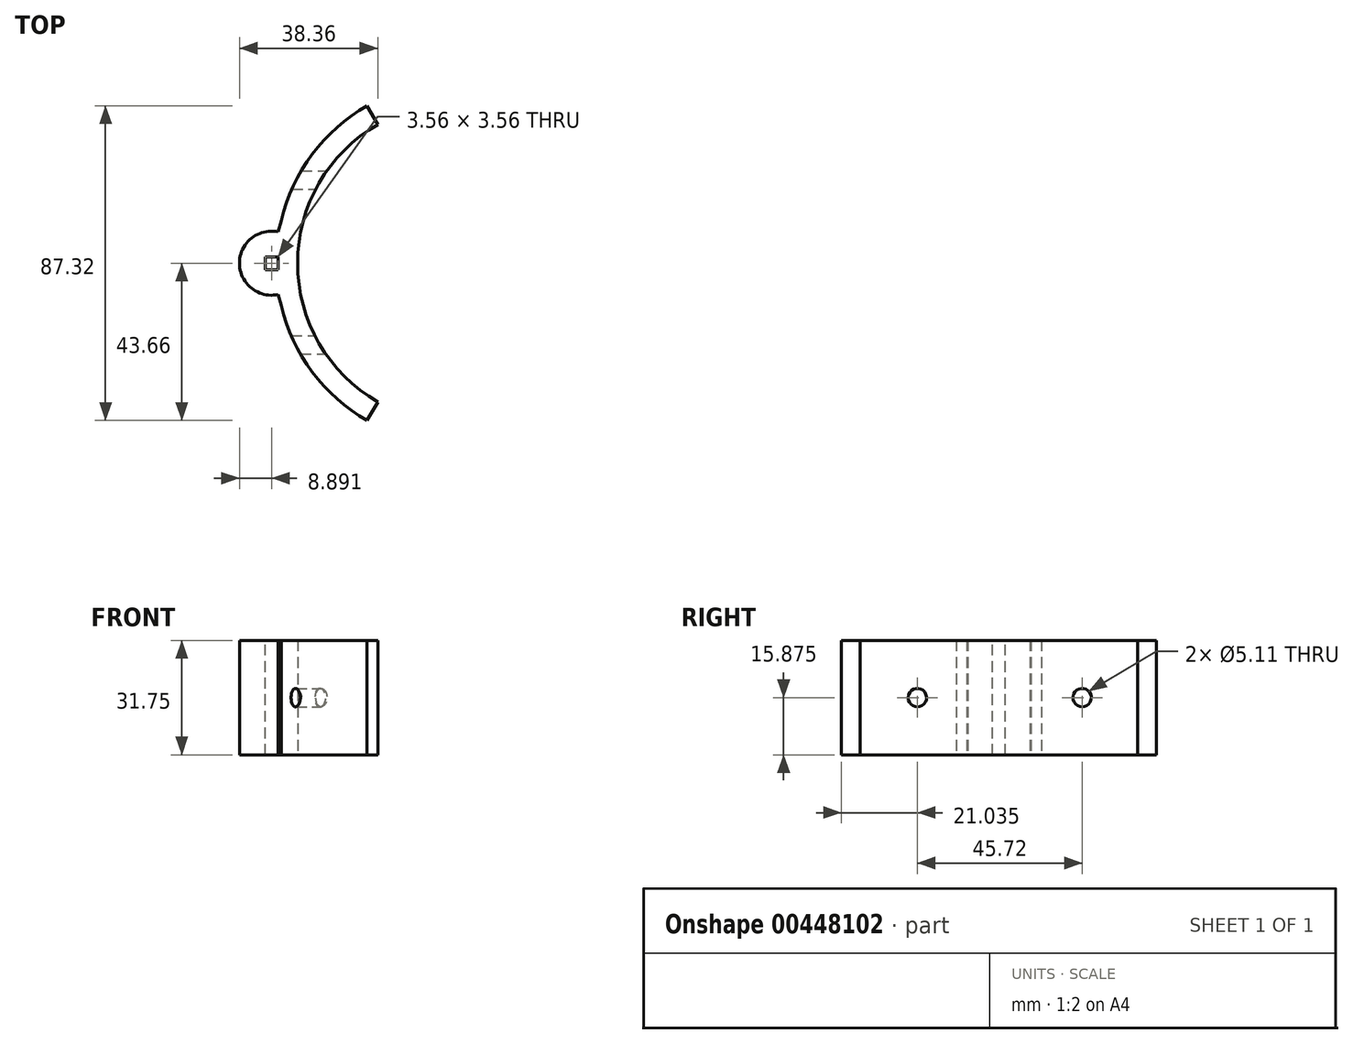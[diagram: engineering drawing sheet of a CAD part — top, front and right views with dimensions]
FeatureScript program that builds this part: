
annotation { "Feature Type Name" : "Feature", "Feature Type Description" : "" }
export const myFeature = defineFeature(function(context is Context, id is Id, definition is map)
    precondition{}
    {
        {
            var Q0;
            Q0=qCreatedBy(makeId("Top.planeOp"),FACE);
            var sketch = newSketch(context, id + "F0", { "sketchPlane" : qUnion([Q0])});
            skArc(sketch, "E0", {"start": v(-22.22, 38.5) * mm, "mid": v(-44.45, 0) * mm, "end": v(-22.22, -38.5) * mm});
            skLineSegment(sketch, "E1", {"start": v(-44.45, 0) * mm, "end": v(-22.23, 0) * mm, "construction": true});
            skPoint(sketch, "E2.start.orphan", {"position": v(-22.23, 0) * mm});
            skArc(sketch, "E3.0", {"start": v(-25.2, 43.66) * mm, "mid": v(-40.4, 30.16) * mm, "end": v(-49.03, 11.75) * mm});
            skLineSegment(sketch, "E4", {"start": v(-25.2, 43.66) * mm, "end": v(-22.22, 38.5) * mm});
            skLineSegment(sketch, "E5", {"start": v(-22.22, -38.5) * mm, "end": v(-25.2, -43.66) * mm});
            skCircle(sketch, "E6", {"center": v(-51.69, 0) * mm, "radius": 1.27 * mm});
            skPoint(sketch, "E6.centerSnap0", {"position": v(-50.42, 0) * mm});
            skLineSegment(sketch, "E7", {"start": v(-49.8, 8.69) * mm, "end": v(-49.03, 11.75) * mm});
            skLineSegment(sketch, "E8", {"start": v(-49.8, -8.69) * mm, "end": v(-49.03, -11.75) * mm});
            skArc(sketch, "E9.trimOffspring", {"start": v(-49.03, -11.75) * mm, "mid": v(-40.4, -30.16) * mm, "end": v(-25.2, -43.66) * mm});
            skArc(sketch, "E10.0", {"start": v(-49.8, 8.69) * mm, "mid": v(-60.58, 0) * mm, "end": v(-49.8, -8.69) * mm});
            skPoint(sketch, "E11.orphan", {"position": v(-51.69, 1.27) * mm});
            skPoint(sketch, "E12.orphan", {"position": v(-51.69, -1.27) * mm});
            skSolve(sketch);
        }
        {
            var Q0;
            Q0 = qSketchRegion(id + "F0", true);
            extrude(context, id + "F1", {"entities" : qUnion([Q0]), "depth" : 31.75 * mm});
        }
        {
            var Q0;
            Q0=makeQuery(id+"F1.opExtrude","CAP_FACE",FACE,{"disambiguationData":[OSD([sQuery(id+"F0.wireOp",EDGE,"E0"),sQuery(id+"F0.wireOp",EDGE,"E3.0"),sQuery(id+"F0.wireOp",EDGE,"E4"),sQuery(id+"F0.wireOp",EDGE,"E5"),sQuery(id+"F0.wireOp",EDGE,"E6"),sQuery(id+"F0.wireOp",EDGE,"E7"),sQuery(id+"F0.wireOp",EDGE,"E8"),sQuery(id+"F0.wireOp",EDGE,"E9.trimOffspring"),sQuery(id+"F0.wireOp",EDGE,"E10.0")])],"isStart":false});
            var sketch = newSketch(context, id + "F2", { "sketchPlane" : qUnion([Q0])});
            skLineSegment(sketch, "E13.bottom", {"start": v(-49.91, -1.78) * mm, "end": v(-53.47, -1.78) * mm});
            skLineSegment(sketch, "E13.top", {"start": v(-49.91, 1.78) * mm, "end": v(-53.47, 1.78) * mm});
            skLineSegment(sketch, "E13.left", {"start": v(-49.91, -1.78) * mm, "end": v(-49.91, 1.78) * mm});
            skLineSegment(sketch, "E13.right", {"start": v(-53.47, -1.78) * mm, "end": v(-53.47, 1.78) * mm});
            skPoint(sketch, "E13.middle", {"position": v(-51.69, 0) * mm});
            skSolve(sketch);
        }
        {
            var Q0;
            Q0=makeQuery(id+"F2.imprint","IMPRINT",FACE,{"disambiguationData":[TD([[makeQuery(id+"F2.imprint","IMPRINT",EDGE,{"derivedFrom":sQuery(id+"F2.wireOp",EDGE,"E13.bottom")}),-1.0]])]});
            extrude(context, id + "F3", {"entities" : qUnion([Q0]), "operationType" : NewBodyOperationType.REMOVE, "endBound" : BoundingType.UP_TO_NEXT, "oppositeDirection" : true, "depth" : 25.4 * mm});
        }
        {
            var Q0;
            Q0=qCreatedBy(makeId("Right.planeOp"),FACE);
            var sketch = newSketch(context, id + "F4", { "sketchPlane" : qUnion([Q0])});
            skLineSegment(sketch, "E14", {"start": v(0, 31.75) * mm, "end": v(0, 0) * mm, "construction": true});
            skLineSegment(sketch, "E15", {"start": v(-22.62, 15.88) * mm, "end": v(23.1, 15.88) * mm});
            skSolve(sketch);
        }
        {
            var Q0;
            Q0=sQuery(id+"F4.wireOp",VERTEX,"E15.start");
            var Q1;
            Q1=sQuery(id+"F4.wireOp",VERTEX,"E15.end");
            var Q2;
            Q2=makeQuery(id+"F1.opExtrude","SWEPT_BODY",BODY,{"disambiguationData":[OSD([sQuery(id+"F0.wireOp",EDGE,"E0"),sQuery(id+"F0.wireOp",EDGE,"E3.0"),sQuery(id+"F0.wireOp",EDGE,"E4"),sQuery(id+"F0.wireOp",EDGE,"E5"),sQuery(id+"F0.wireOp",EDGE,"E6"),sQuery(id+"F0.wireOp",EDGE,"E7"),sQuery(id+"F0.wireOp",EDGE,"E8"),sQuery(id+"F0.wireOp",EDGE,"E9.trimOffspring"),sQuery(id+"F0.wireOp",EDGE,"E10.0")])]});
            hole(context, id + "F5", {"style" : HoleStyle.SIMPLE, "endStyle" : HoleEndStyle.THROUGH, "holeDiameter" : 5.1 * mm, "isTappedThrough" : true, "tappedDepth" : 12.7 * mm, "tapClearance" : 3, "locations" : qUnion([Q0, Q1]), "scope" : qUnion([Q2])});
        }
    });
